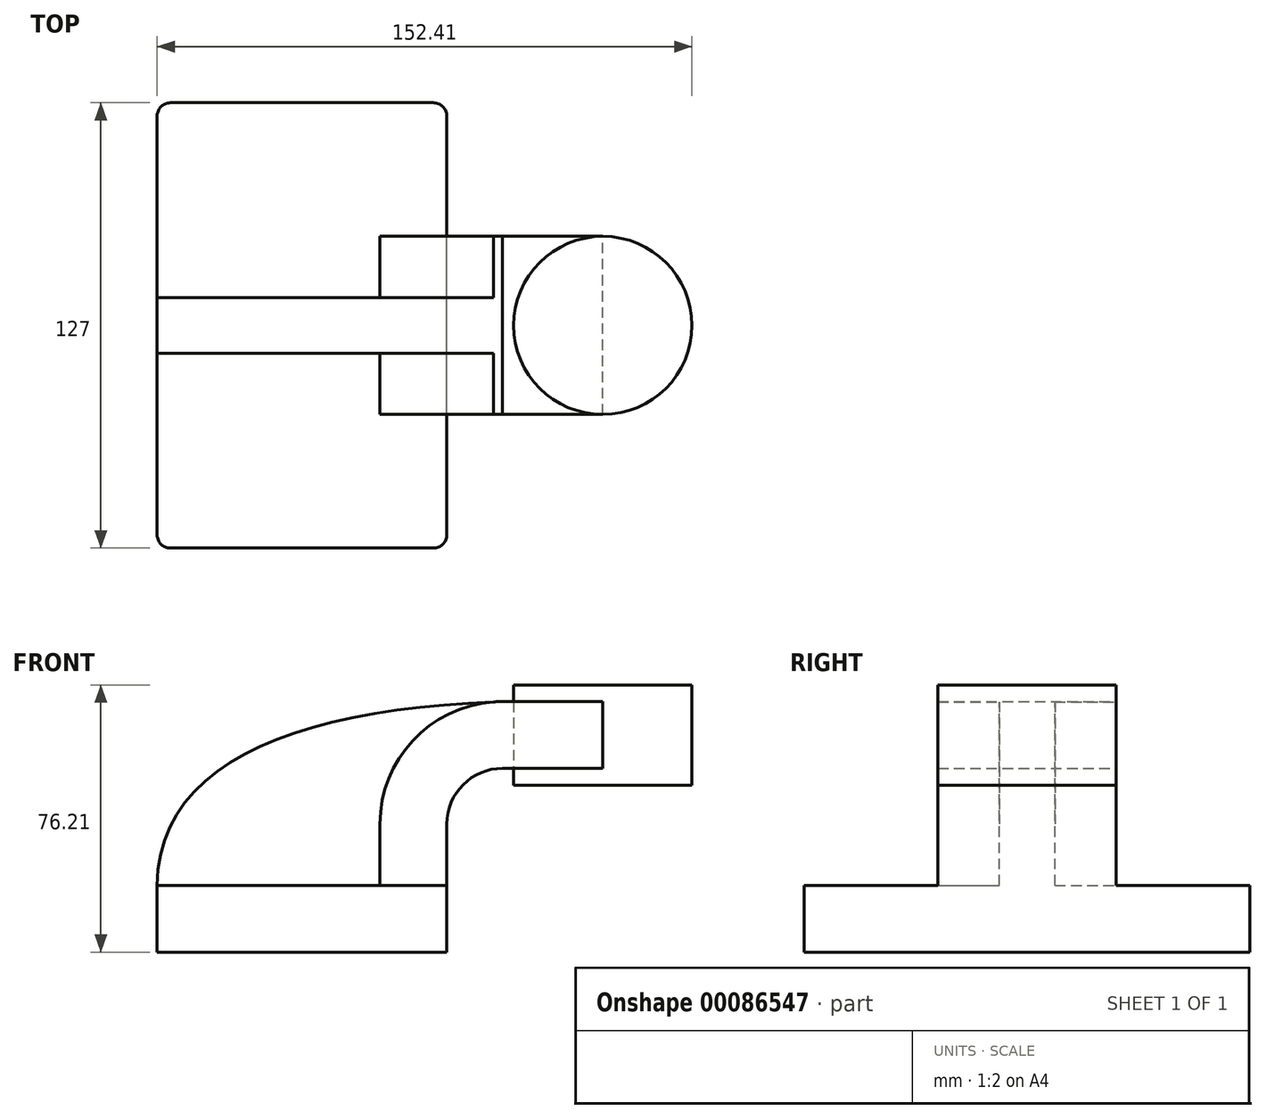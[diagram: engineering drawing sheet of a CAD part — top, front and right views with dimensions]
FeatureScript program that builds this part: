
annotation { "Feature Type Name" : "Feature", "Feature Type Description" : "" }
export const myFeature = defineFeature(function(context is Context, id is Id, definition is map)
    precondition{}
    {
        {
            var Q0;
            Q0=qCreatedBy(makeId("Front.planeOp"),FACE);
            var sketch = newSketch(context, id + "F0", { "sketchPlane" : qUnion([Q0])});
            skLineSegment(sketch, "E0.bottom", {"start": v(-41.28, -9.52) * mm, "end": v(41.28, -9.52) * mm});
            skLineSegment(sketch, "E0.top", {"start": v(-41.28, 9.53) * mm, "end": v(41.28, 9.53) * mm});
            skLineSegment(sketch, "E0.left", {"start": v(-41.28, -9.52) * mm, "end": v(-41.28, 9.53) * mm});
            skLineSegment(sketch, "E0.right", {"start": v(41.28, -9.53) * mm, "end": v(41.28, 9.52) * mm});
            skPoint(sketch, "E0.middle", {"position": v(0, 0) * mm});
            skLineSegment(sketch, "E1.bottom", {"start": v(60.32, 38.1) * mm, "end": v(111.12, 38.1) * mm});
            skLineSegment(sketch, "E1.top", {"start": v(60.32, 66.68) * mm, "end": v(111.12, 66.68) * mm});
            skLineSegment(sketch, "E1.left", {"start": v(60.32, 38.1) * mm, "end": v(60.32, 66.67) * mm});
            skLineSegment(sketch, "E1.right", {"start": v(111.12, 38.1) * mm, "end": v(111.12, 66.67) * mm});
            skPoint(sketch, "E1.middle", {"position": v(85.72, 52.39) * mm});
            skLineSegment(sketch, "E2", {"start": v(41.28, 9.53) * mm, "end": v(41.28, 26.97) * mm});
            skArc(sketch, "E3", {"start": v(41.27, 26.97) * mm, "mid": v(45.93, 38.22) * mm, "end": v(57.18, 42.88) * mm});
            skLineSegment(sketch, "E4", {"start": v(57.18, 42.88) * mm, "end": v(85.73, 42.88) * mm});
            skLineSegment(sketch, "E5.0", {"start": v(57.18, 61.93) * mm, "end": v(85.73, 61.93) * mm});
            skArc(sketch, "E5.1", {"start": v(22.22, 26.97) * mm, "mid": v(32.46, 51.69) * mm, "end": v(57.18, 61.93) * mm});
            skLineSegment(sketch, "E5.2", {"start": v(22.22, 9.53) * mm, "end": v(22.22, 26.97) * mm});
            skFitSpline(sketch, "E6", {"points": [v(-41.28, 9.53) * mm, v(57.18, 61.93) * mm], "startDerivative": vector(0.85, 107.03) * mm, "endDerivative": vector(171.53, 5.67) * mm});
            skLineSegment(sketch, "E7", {"start": v(85.72, 38.1) * mm, "end": v(85.72, 66.68) * mm});
            skSolve(sketch);
        }
        {
            var Q0;
            Q0=makeQuery(id+"F0.imprint","IMPRINT",FACE,{"disambiguationData":[TD([[makeQuery(id+"F0.imprint","IMPRINT",EDGE,{"derivedFrom":sQuery(id+"F0.wireOp",EDGE,"E0.bottom")}),1.0]])]});
            extrude(context, id + "F1", {"entities" : qUnion([Q0]), "endBound" : BoundingType.SYMMETRIC, "depth" : 127 * mm});
        }
        {
            var Q0;
            {var subQ1=sQuery(id+"F0.wireOp",EDGE,"E2");Q0=makeQuery(id+"F0.imprint","IMPRINT",FACE,{"disambiguationData":[TD([[makeQuery(id+"F0.imprint","IMPRINT",EDGE,{"derivedFrom":subQ1}),1.0]])]});}
            var Q1;
            {var subQ0=sQuery(id+"F0.wireOp",EDGE,"E4");var subQ1=sQuery(id+"F0.wireOp",EDGE,"E1.left");var subQ2=makeQuery(id+"F0.imprint","INTERSECT",VERTEX,{"derivedFrom":[subQ1,subQ0]});Q1=makeQuery(id+"F0.imprint","IMPRINT",FACE,{"disambiguationData":[TD([[makeQuery(id+"F0.imprint","IMPRINT",EDGE,{"disambiguationData":[TD([[subQ2,-1.0]])],"derivedFrom":subQ1}),-1.0]])]});}
            extrude(context, id + "F2", {"entities" : qUnion([Q0, Q1]), "operationType" : NewBodyOperationType.ADD, "endBound" : BoundingType.SYMMETRIC, "depth" : 50.8 * mm});
        }
        {
            var Q0;
            {var subQ3=sQuery(id+"F0.wireOp",EDGE,"E5.2");Q0=makeQuery(id+"F0.imprint","IMPRINT",FACE,{"disambiguationData":[TD([[makeQuery(id+"F0.imprint","IMPRINT",EDGE,{"derivedFrom":subQ3}),1.0]])]});}
            extrude(context, id + "F3", {"entities" : qUnion([Q0]), "operationType" : NewBodyOperationType.ADD, "endBound" : BoundingType.SYMMETRIC, "depth" : 15.88 * mm});
        }
        {
            var Q0;
            {var subQ0=sQuery(id+"F0.wireOp",EDGE,"E1.right");Q0=makeQuery(id+"F0.imprint","IMPRINT",FACE,{"disambiguationData":[TD([[makeQuery(id+"F0.imprint","IMPRINT",EDGE,{"derivedFrom":subQ0}),1.0]])]});}
            var Q1;
            Q1=sQuery(id+"F0.wireOp",EDGE,"E7");
            revolve(context, id + "F4", {"entities" : qUnion([Q0]), "axis" : qUnion([Q1]), "revolveType" : RevolveType.FULL});
        }
        {
            var Q0;
            Q0=makeQuery(id+"F1.opExtrude","CAP_EDGE",EDGE,{"disambiguationData":[OSD([sQuery(id+"F0.wireOp",EDGE,"E0.left")])],"isStart":false});
            var Q1;
            Q1=makeQuery(id+"F1.opExtrude","CAP_EDGE",EDGE,{"disambiguationData":[OSD([sQuery(id+"F0.wireOp",EDGE,"E0.right")])],"isStart":false});
            var Q2;
            Q2=makeQuery(id+"F1.opExtrude","CAP_EDGE",EDGE,{"disambiguationData":[OSD([sQuery(id+"F0.wireOp",EDGE,"E0.right")])],"isStart":true});
            var Q3;
            Q3=makeQuery(id+"F1.opExtrude","CAP_EDGE",EDGE,{"disambiguationData":[OSD([sQuery(id+"F0.wireOp",EDGE,"E0.left")])],"isStart":true});
            fillet(context, id + "F5", {"entities" : qUnion([Q0, Q1, Q2, Q3]), "radius" : 3.8 * mm, "tangentPropagation" : true, "allowEdgeOverflow" : false});
        }
    });
